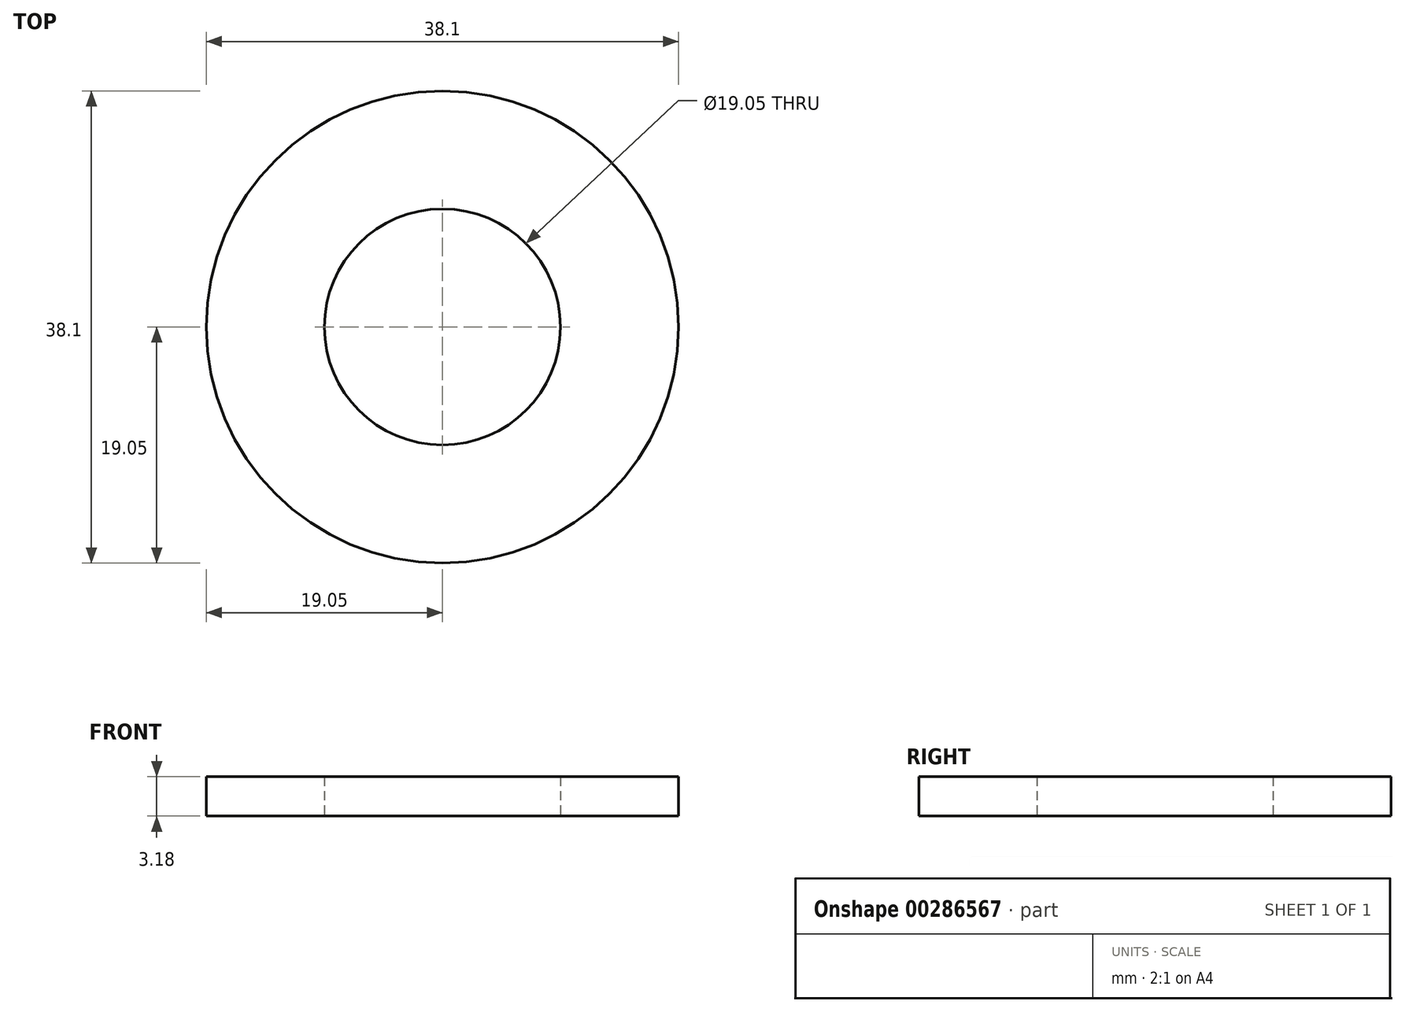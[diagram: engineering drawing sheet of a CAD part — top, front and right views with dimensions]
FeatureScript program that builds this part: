
annotation { "Feature Type Name" : "Feature", "Feature Type Description" : "" }
export const myFeature = defineFeature(function(context is Context, id is Id, definition is map)
    precondition{}
    {
        {
            var Q0;
            Q0=qCreatedBy(makeId("Top.planeOp"),FACE);
            var sketch = newSketch(context, id + "F0", { "sketchPlane" : qUnion([Q0])});
            skCircle(sketch, "E0", {"center": v(0, 0) * mm, "radius": 9.53 * mm});
            skCircle(sketch, "E1", {"center": v(0, 0) * mm, "radius": 19.05 * mm});
            skSolve(sketch);
        }
        {
            var Q0;
            Q0=qSketchRegion(id+"F0",true);
            extrude(context, id + "F1", {"entities" : qUnion([Q0]), "depth" : 3.17 * mm});
        }
        {
            var Q0;
            Q0=qSketchRegion(id+"F0",true);
            extrude(context, id + "F2", {"entities" : qUnion([Q0]), "operationType" : NewBodyOperationType.ADD, "depth" : 3.17 * mm});
        }
    });
